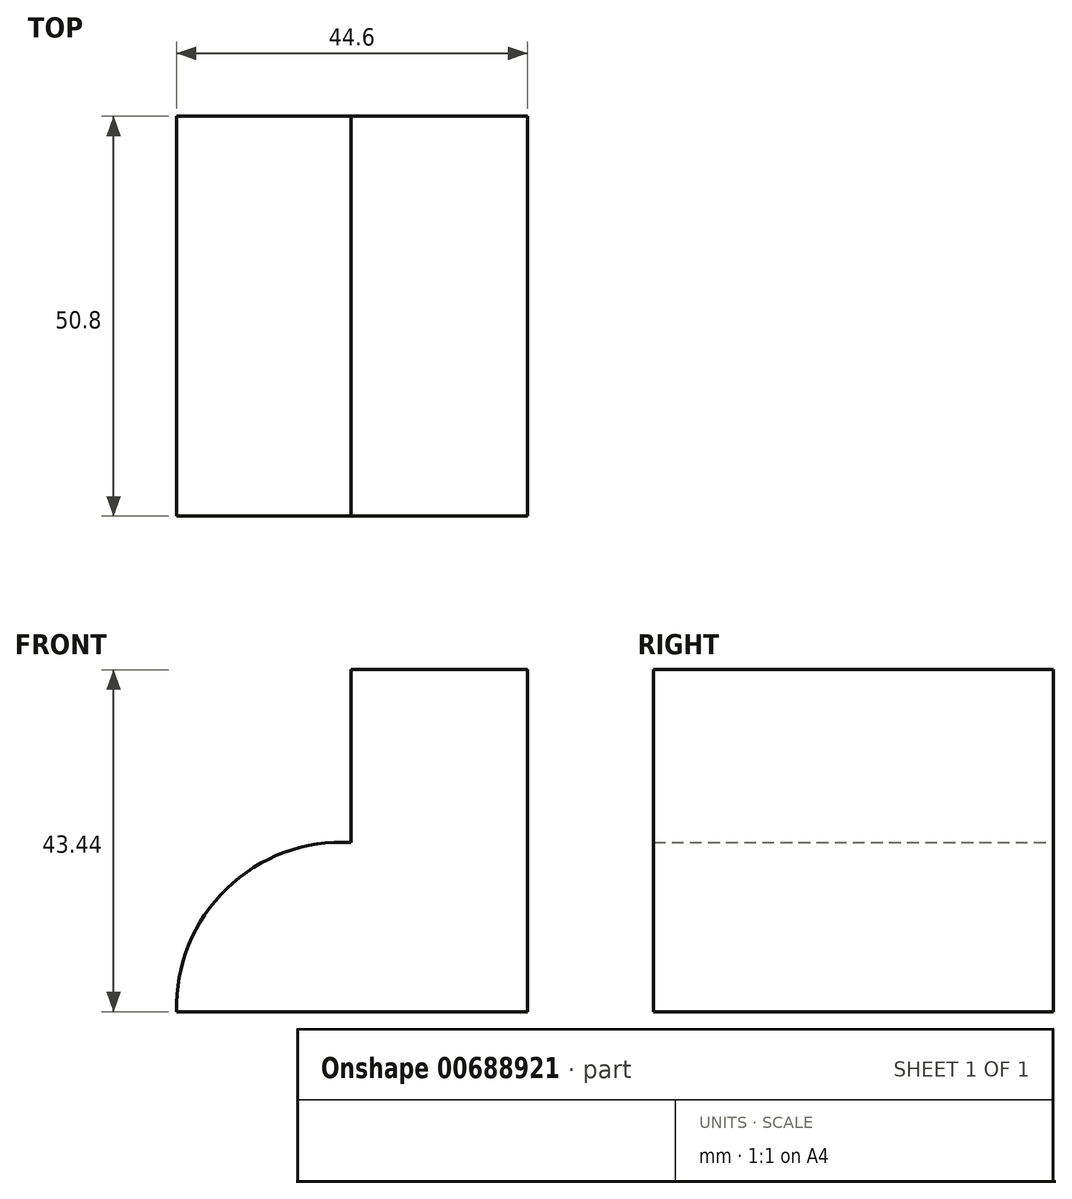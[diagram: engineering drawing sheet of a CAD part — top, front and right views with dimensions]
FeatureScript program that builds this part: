
annotation { "Feature Type Name" : "Feature", "Feature Type Description" : "" }
export const myFeature = defineFeature(function(context is Context, id is Id, definition is map)
    precondition{}
    {
        {
            var Q0;
            Q0=qCreatedBy(makeId("Front.planeOp"),FACE);
            var sketch = newSketch(context, id + "F0", { "sketchPlane" : qUnion([Q0])});
            skLineSegment(sketch, "E0", {"start": v(-44.59, 0) * mm, "end": v(0, 0) * mm});
            skLineSegment(sketch, "E1", {"start": v(0, 0) * mm, "end": v(0, 43.44) * mm});
            skLineSegment(sketch, "E2", {"start": v(0, 43.44) * mm, "end": v(-22.44, 43.44) * mm});
            skLineSegment(sketch, "E3", {"start": v(-22.44, 43.44) * mm, "end": v(-22.44, 21.48) * mm});
            skArc(sketch, "E4", {"start": v(-22.44, 21.48) * mm, "mid": v(-38.25, 15.63) * mm, "end": v(-44.59, 0) * mm});
            skSolve(sketch);
        }
        {
            var Q0;
            Q0 = qSketchRegion(id + "F0", true);
            extrude(context, id + "F1", {"entities" : qUnion([Q0]), "depth" : 50.8 * mm, "offsetDistance" : 25.4 * mm});
        }
    });
